# Revit family: Hängestiel - US 7 K 20 FT SO
name_source: partatom
category: Generic Models
revit_build: Autodesk Revit 2017 (Build: 20190508_0315(x64)
units: mm (PartAtom-declared; Revit-internal decimal feet)

## family parameters
Always vertical = Yes
Can host rebar = No
Cut with Voids When Loaded = No
Part Type = Normal
Room Calculation Point = No
Round Connector Dimension = Use Diameter
Shared = No
Work Plane-Based = No

## types (10) — shared parameters
Cut's space = 50 mm  [stored 0.164042 ft]
Manufacturer = OBO BETTERMANN
Material = Hot dip galvanised
URL = http://www.obo.bettermann.com

## per-type parameters (varying)
| type | Cut's number | GTIN | Length | Manufacturer Art.No. |
| US 7 K 30 FT SO | 6 | 4012195019688 | 300 mm | 7193647 |
| US 7 K 20 FT SO | 4 | 4012195019664 | 200 mm  [stored 0.656168 ft] | 7193645 |
| US 7 K 40 FT SO | 8 | 4012195019725 | 400 mm  [stored 1.31234 ft] | 7193649 |
| US 7 K 50 FT SO | 10 | 4012195019787 | 500 mm  [stored 1.64042 ft] | 7193651 |
| US 7 K 60 FT SO | 12 | 4012195019800 | 600 mm | 7193653 |
| US 7 K 70 FT SO | 14 | 4012195019848 | 700 mm  [stored 2.29659 ft] | 7193655 |
| US 7 K 80 FT SO | 16 | 4012195019909 | 800 mm  [stored 2.62467 ft] | 7193657 |
| US 7 K 90 FT SO | 18 | 4012195019923 | 900 mm  [stored 2.95276 ft] | 7193659 |
| US 7 K 100 FT SO | 20 | 4012196176175 | 1000 mm  [stored 3.28084 ft] | 7193661 |
| US 7 K 120 FT SO | 24 | 4012195020028 | 1200 mm | 7193665 |

note: column(s) folded — value = type name in every type: Article Type

note: [stored X ft] marks values corroborated as IEEE doubles in the binary element streams (Revit-internal decimal feet)

## geometry (parser evidence)
native form markers: Sweep x2
no freeform markers — native parametric forms only
